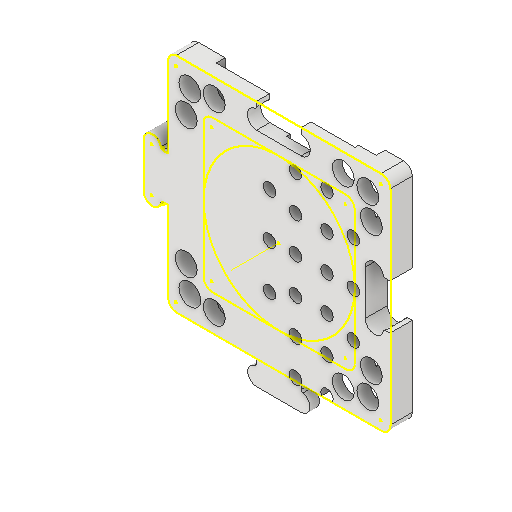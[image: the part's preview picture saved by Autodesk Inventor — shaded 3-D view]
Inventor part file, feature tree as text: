
AUTODESK INVENTOR PART (.ipt)
format: ipt  version: 2022 (Build 260153000, 153)  size: 479,232 bytes
history: native  units: mm
features: other x6, sketch x5, extrude x4, projected_geometry x3, reference x3, pattern_linear x2
ambient origin geometry x8: Origin, YZ Plane, XZ Plane, XY Plane, X Axis, Y Axis, Z Axis, Center Point
bodies: Body1 (feature_tree)
feature tree (23):
  other  "10_Base_puzzle_v3.ipt"
  extrude  "Extrusion5"  Depth=10.0mm TaperAngle=0.0deg
  extrude  "Extrusion6"  Depth=10.0mm
  extrude  "Extrusion8"  Depth=0.7mm
  pattern_linear  "Rechteckige Anordnung2"  Spacing1=0.15mm  [1 undecoded]
  extrude  "Extrusion9"  Depth=10.0mm
  pattern_linear  "Rechteckige Anordnung3"  Spacing1=2.8mm  [1 undecoded]
  other  "Volumenkörper1::10_Base_puzzle_v3.ipt"
  other  "TaggingFeature1"
  sketch  "Sketch27"  dims[d72=0.0mm d73=0.15mm d74=2.8mm d75=2.8mm d76=10.0mm d77=0.0mm d78=60.0mm d80=8.0mm d81=2.8mm d82=2.8mm d83=10.0mm d84=0.0mm d85=30.0mm d87=10.0mm]
  sketch  "Sketch6"  dims[d19=10.0mm d20=10.0mm d21=0.0mm]
  projected_geometry  "Projected Loop1"
  sketch  "Sketch7"  dims[d26=10.0mm d27=0.0mm d65=0.7mm]
  reference  "Referenz15"
  sketch  "Skizze12"  dims[d66=0.7mm d67=0.7mm]
  reference  "Referenz16"
  reference  "Referenz17"
  sketch  "Skizze13"  dims[d71=6.0mm]
  projected_geometry  "Projizierte Kontur10"
  projected_geometry  "Projizierte Kontur11"
  other  "Assembly_Cube_Dichroic_Beamsplitter_multi_motorized_25x35_linearmotor_v3.iam"
  other  "Assebmly_Linear_Stepper_90mm:1"
  other  "00_Linear_Stepper_90mm:1"
note: 2 required parameter values undecoded (feature->parameter linkage not recoverable at this tier; creation-order binding heuristic only, values carry confidence <= 0.55)
